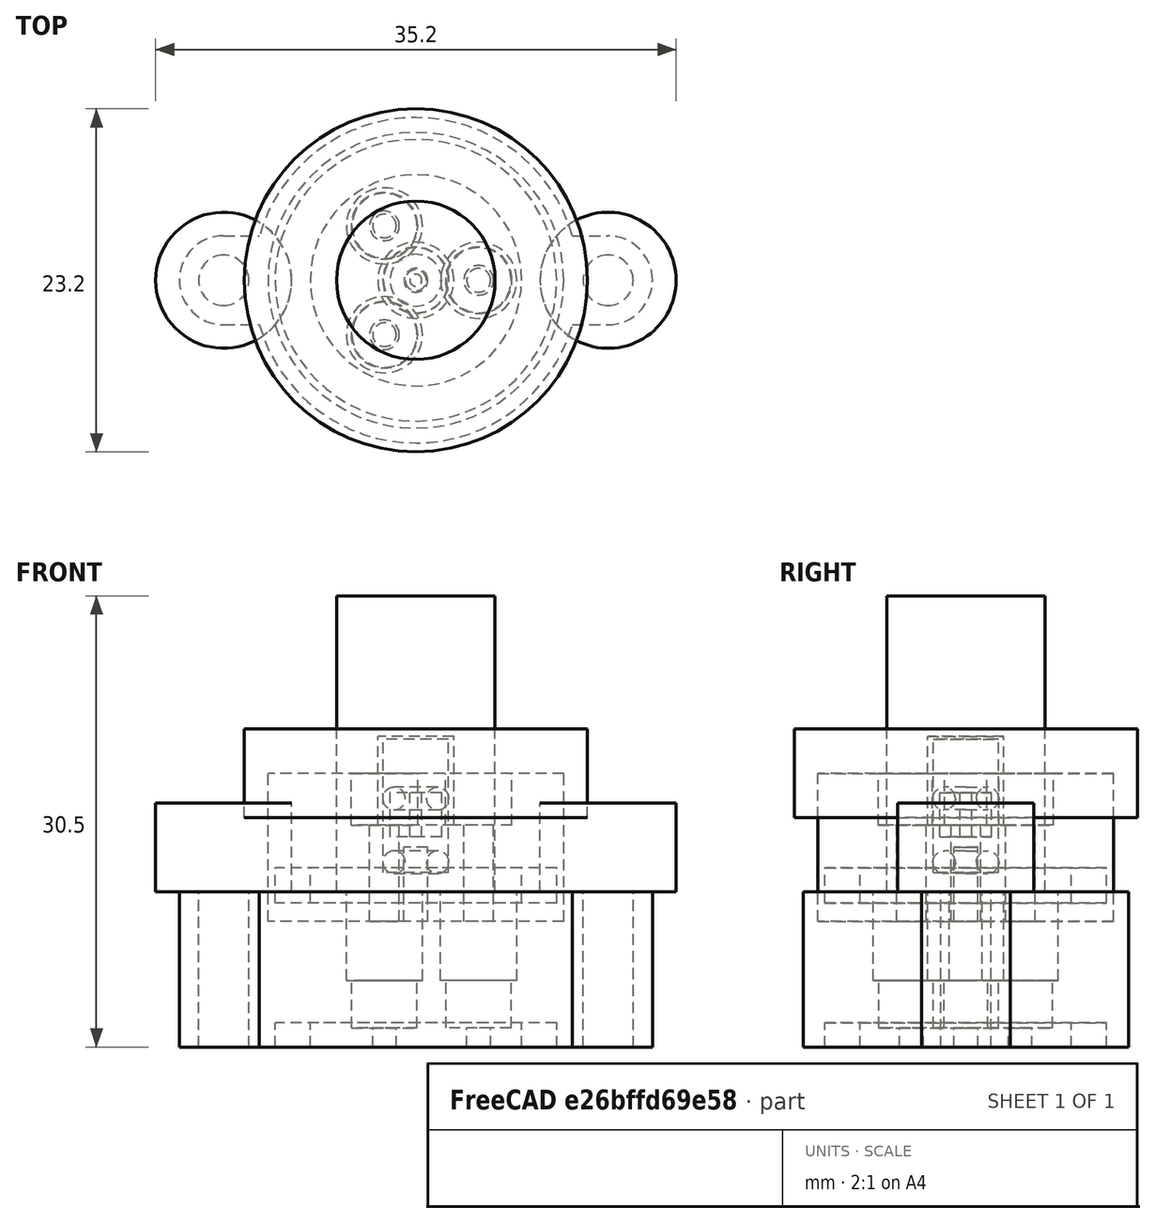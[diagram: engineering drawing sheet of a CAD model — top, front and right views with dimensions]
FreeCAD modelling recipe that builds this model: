
FCSTD DOCUMENT  (FreeCAD 0.17R13509 (Git))
Label: ceramic_wire_feedthroughs_insert_tall
License: All rights reserved
LicenseURL: http://en.wikipedia.org/wiki/All_rights_reserved
objects: Part::Cylinder×45, Part::MultiFuse×10, Part::Cut×9, Part::Box×6, Part::FeaturePython×4, Part::Feature×2, App::FeaturePython×1
note: 76 computed .brp shape members not serialized (recipe doc carries the construction recipe); baked Part::Feature solids carry a one-line shape summary decoded from their .brp

FEATURE [Part::Cylinder] Cylinder155  label="Cylinder009"
  Angle = 360
  AttacherType = Attacher::AttachEngine3D
  Height = 2.38125
  Radius = 9.525
  expr: Radius = 3 / 4 * 25.399999999999999 / 2
  expr: Height = 3 / 32 * 25.399999999999999
FEATURE [Part::Cylinder] Cylinder154  label="Cylinder008"
  Angle = 360
  AttacherType = Attacher::AttachEngine3D
  Height = 2.38125
  Radius = 7.14375
  expr: Radius = 9 / 16 * 25.399999999999999 / 2
  expr: Height = 3 / 32 * 25.399999999999999
FEATURE [Part::Feature] Part__Feature001  label="TopOring"
  Placement = pos=(0,0,6.3) rot=(0,0,1;0rad)
  shape: bbox 4.839 x 4.839 x 1.524 mm, 4 faces (baked)
FEATURE [Part::Feature] Part__Feature002  label="BottomOring"
  Placement = pos=(0,0,2) rot=(0,0,1;0rad)
  shape: bbox 4.839 x 4.839 x 1.524 mm, 4 faces (baked)
FEATURE [Part::Cylinder] Cylinder153  label="Body"
  Angle = 360
  AttacherType = Attacher::AttachEngine3D
  Height = 10
  Placement = pos=(0,0,-2) rot=(0,0,1;0rad)
  Radius = 10
FEATURE [Part::Cut] Cut019  label="Oring"
  Base = -> Cylinder155
  Placement = pos=(0,0,-0.75) rot=(0,0,1;0rad)
  Tool = -> Cylinder154
FEATURE [Part::Cylinder] Cylinder147  label="ThreadedSection"
  Angle = 360
  AttacherType = Attacher::AttachEngine3D
  Height = 1
  Placement = pos=(0,0,4.5) rot=(0,0,1;0rad)
  Radius = 1
FEATURE [Part::Cylinder] Cylinder149  label="FTBead"
  Angle = 360
  AttacherType = Attacher::AttachEngine3D
  Height = 3
  Placement = pos=(0,0,2.7) rot=(0,0,1;0rad)
  Radius = 1.75
  expr: Radius = 3.5 / 2
FEATURE [Part::Cylinder] Cylinder152  label="RFFeeds005"
  Angle = 360
  AttacherType = Attacher::AttachEngine3D
  Height = 20
  Radius = 5.35813
  expr: Placement.Base.x = 0
FEATURE [Part::Cylinder] Cylinder156  label="BottomWireOutlet"
  Angle = 360
  AttacherType = Attacher::AttachEngine3D
  Height = 14
  Placement = pos=(0,0,-7) rot=(0,0,1;0rad)
  Radius = 1
FEATURE [Part::Cylinder] Cylinder157  label="SealSubtraction"
  Angle = 360
  AttacherType = Attacher::AttachEngine3D
  Height = 7
  Placement = pos=(0,0,4.5) rot=(0,0,1;0rad)
  Radius = 2.25
FEATURE [Part::MultiFuse] Fusion
  Placement = pos=(4.25,0,0) rot=(0,0,1;0rad)
  Shapes = -> [Cylinder147,Cylinder157,Cylinder156]
FEATURE [Part::FeaturePython] Array  label="SealArray"  # Draft array (typed FeaturePython)
  Angle = 360
  ArrayType = 1
  Axis = (0,0,1)
  Base = -> Fusion
  Center = (0,0,0)
  Fuse = false
  IntervalAxis = (0,0,0)
  IntervalX = (1,0,0)
  IntervalY = (0,1,0)
  IntervalZ = (0,0,0)
  NumberPolar = 3
  NumberX = 2
  NumberY = 2
  NumberZ = 1
FEATURE [Part::Cylinder] Cylinder159  label="FTBeadHole"
  Angle = 360
  AttacherType = Attacher::AttachEngine3D
  Height = 17
  Radius = 0.405
  expr: Radius = 0.81000000000000005 / 2
FEATURE [Part::Cut] Cut020
  Base = -> Cylinder149
  Placement = pos=(0,0,1) rot=(0,0,1;0rad)
  Tool = -> Cylinder159
FEATURE [Part::Cylinder] Cylinder160  label="Cylinder010"
  Angle = 360
  AttacherType = Attacher::AttachEngine3D
  Height = 2.38125
  Radius = 9.525
  expr: Radius = 3 / 4 * 25.399999999999999 / 2
  expr: Height = 3 / 32 * 25.399999999999999
FEATURE [Part::Cylinder] Cylinder161  label="WireFeedsMount003"
  Angle = 360
  AttacherType = Attacher::AttachEngine3D
  Height = 11
  Placement = pos=(-13,0,0) rot=(0,0,1;0rad)
  Radius = 1.7
FEATURE [Part::Cylinder] Cylinder162  label="ThreadedSection001"
  Angle = 360
  AttacherType = Attacher::AttachEngine3D
  Height = 6
  Placement = pos=(0,0,4.5) rot=(0,0,1;0rad)
  Radius = 2.575
  expr: Radius = 5.1500000000000004 / 2
FEATURE [Part::Cylinder] Cylinder163  label="Cylinder011"
  Angle = 360
  AttacherType = Attacher::AttachEngine3D
  Height = 2.38125
  Radius = 7.14375
  expr: Radius = 9 / 16 * 25.399999999999999 / 2
  expr: Height = 3 / 32 * 25.399999999999999
FEATURE [Part::Cut] Cut022  label="Oring001"
  Base = -> Cylinder160
  Placement = pos=(0,0,-0.75) rot=(0,0,1;0rad)
  Tool = -> Cylinder163
FEATURE [Part::Cylinder] Cylinder164  label="Body001"
  Angle = 360
  AttacherType = Attacher::AttachEngine3D
  Height = 10.5
  Radius = 11
FEATURE [Part::Cylinder] Cylinder165  label="WireFeedsMount004"
  Angle = 360
  AttacherType = Attacher::AttachEngine3D
  Height = 11
  Placement = pos=(13,0,0) rot=(0,0,1;0rad)
  Radius = 1.7
FEATURE [Part::Cylinder] Cylinder166  label="BottomWireOutlet001"
  Angle = 360
  AttacherType = Attacher::AttachEngine3D
  Height = 5
  Placement = pos=(0,0,-2) rot=(0,0,1;0rad)
  Radius = 0.8
FEATURE [Part::Cylinder] Cylinder167  label="SealSubtraction001"
  Angle = 360
  AttacherType = Attacher::AttachEngine3D
  Height = 9
  Placement = pos=(0,0,1.3) rot=(0,0,1;0rad)
  Radius = 2.2
FEATURE [Part::Box] Box002  label="MountCube003"
  AttacherType = Attacher::AttachEngine3D
  Height = 10.5
  Length = 3
  Placement = pos=(10,-3,0) rot=(0,0,1;0rad)
  Width = 6
FEATURE [Part::Box] Box003  label="MountCube004"
  AttacherType = Attacher::AttachEngine3D
  Height = 10.5
  Length = 3
  Placement = pos=(-13,-3,0) rot=(0,0,1;0rad)
  Width = 6
FEATURE [Part::MultiFuse] Fusion004
  Placement = pos=(4.25,0,0) rot=(0,0,1;0rad)
  Shapes = -> [Cylinder162,Cylinder167,Cylinder166]
FEATURE [Part::Cylinder] Cylinder168  label="MountFlange003"
  Angle = 360
  AttacherType = Attacher::AttachEngine3D
  Height = 10.5
  Placement = pos=(-13,0,0) rot=(0,0,1;0rad)
  Radius = 3
FEATURE [Part::Cylinder] Cylinder169  label="MountFlange004"
  Angle = 360
  AttacherType = Attacher::AttachEngine3D
  Height = 10.5
  Placement = pos=(13,0,0) rot=(0,0,1;0rad)
  Radius = 3
FEATURE [Part::MultiFuse] Fusion003
  Shapes = -> [Cylinder169,Box002,Box003,Cylinder168,Cylinder164]
FEATURE [Part::FeaturePython] Array001  label="SealArray001"  # Draft array (typed FeaturePython)
  Angle = 360
  ArrayType = 1
  Axis = (0,0,1)
  Base = -> Fusion004
  Center = (0,0,0)
  Fuse = false
  IntervalAxis = (0,0,0)
  IntervalX = (1,0,0)
  IntervalY = (0,1,0)
  IntervalZ = (0,0,0)
  NumberPolar = 3
  NumberX = 2
  NumberY = 2
  NumberZ = 1
FEATURE [Part::MultiFuse] Fusion005
  Shapes = -> [Cylinder165,Cylinder161,Cut022,Array001]
FEATURE [Part::Cut] Cut021
  Base = -> Fusion003
  Placement = pos=(0,0,-10.5) rot=(0,0,1;0rad)
  Tool = -> Fusion005
FEATURE [Part::Cylinder] Cylinder170  label="Cylinder012"
  Angle = 360
  AttacherType = Attacher::AttachEngine3D
  Height = 2.38125
  Radius = 9.525
  expr: Radius = 3 / 4 * 25.399999999999999 / 2
  expr: Height = 3 / 32 * 25.399999999999999
FEATURE [Part::Cylinder] Cylinder171  label="WireFeedsMount005"
  Angle = 360
  AttacherType = Attacher::AttachEngine3D
  Height = 11
  Placement = pos=(-13,0,0) rot=(0,0,1;0rad)
  Radius = 1.7
FEATURE [Part::Cylinder] Cylinder172  label="ThreadedSection002"
  Angle = 360
  AttacherType = Attacher::AttachEngine3D
  Height = 6
  Placement = pos=(0,0,4.5) rot=(0,0,1;0rad)
  Radius = 2.575
  expr: Radius = 5.1500000000000004 / 2
FEATURE [Part::Cylinder] Cylinder173  label="Cylinder013"
  Angle = 360
  AttacherType = Attacher::AttachEngine3D
  Height = 2.38125
  Radius = 7.14375
  expr: Radius = 9 / 16 * 25.399999999999999 / 2
  expr: Height = 3 / 32 * 25.399999999999999
FEATURE [Part::Cut] Cut024  label="Oring002"
  Base = -> Cylinder170
  Placement = pos=(0,0,-0.75) rot=(0,0,1;0rad)
  Tool = -> Cylinder173
FEATURE [Part::Cylinder] Cylinder174  label="Body002"
  Angle = 360
  AttacherType = Attacher::AttachEngine3D
  Height = 10.5
  Radius = 11
FEATURE [Part::Cylinder] Cylinder175  label="WireFeedsMount006"
  Angle = 360
  AttacherType = Attacher::AttachEngine3D
  Height = 11
  Placement = pos=(13,0,0) rot=(0,0,1;0rad)
  Radius = 1.7
FEATURE [Part::Cylinder] Cylinder176  label="BottomWireOutlet002"
  Angle = 360
  AttacherType = Attacher::AttachEngine3D
  Height = 5
  Placement = pos=(0,0,-2) rot=(0,0,1;0rad)
  Radius = 0.8
FEATURE [Part::Cylinder] Cylinder177  label="SealSubtraction002"
  Angle = 360
  AttacherType = Attacher::AttachEngine3D
  Height = 9
  Placement = pos=(0,0,1.3) rot=(0,0,1;0rad)
  Radius = 2.2
FEATURE [Part::Box] Box004  label="MountCube005"
  AttacherType = Attacher::AttachEngine3D
  Height = 10.5
  Length = 3
  Placement = pos=(10,-3,0) rot=(0,0,1;0rad)
  Width = 6
FEATURE [App::FeaturePython] SetupSheet002  # Path/CAM operation (typed FeaturePython)
  ClearanceHeightExpression = StartDepth+SetupSheet.ClearanceHeightOffset
  ClearanceHeightOffset = 5
  FinalDepthExpression = OpFinalDepth
  HorizRapid = 0
  SafeHeightExpression = StartDepth+SetupSheet.SafeHeightOffset
  SafeHeightOffset = 3
  StartDepthExpression = OpStartDepth
  StepDownExpression = OpToolDiameter
  VertRapid = 0
FEATURE [Part::Box] Box005  label="MountCube006"
  AttacherType = Attacher::AttachEngine3D
  Height = 10.5
  Length = 3
  Placement = pos=(-13,-3,0) rot=(0,0,1;0rad)
  Width = 6
FEATURE [Part::MultiFuse] Fusion007
  Placement = pos=(4.25,0,0) rot=(0,0,1;0rad)
  Shapes = -> [Cylinder172,Cylinder177,Cylinder176]
FEATURE [Part::Cylinder] Cylinder178  label="MountFlange005"
  Angle = 360
  AttacherType = Attacher::AttachEngine3D
  Height = 10.5
  Placement = pos=(-13,0,0) rot=(0,0,1;0rad)
  Radius = 3
FEATURE [Part::Cylinder] Cylinder179  label="MountFlange006"
  Angle = 360
  AttacherType = Attacher::AttachEngine3D
  Height = 10.5
  Placement = pos=(13,0,0) rot=(0,0,1;0rad)
  Radius = 3
FEATURE [Part::MultiFuse] Fusion006
  Shapes = -> [Cylinder179,Box004,Box005,Cylinder178,Cylinder174]
FEATURE [Part::FeaturePython] Array002  label="SealArray002"  # Draft array (typed FeaturePython)
  Angle = 360
  ArrayType = 1
  Axis = (0,0,1)
  Base = -> Fusion007
  Center = (0,0,0)
  Fuse = false
  IntervalAxis = (0,0,0)
  IntervalX = (1,0,0)
  IntervalY = (0,1,0)
  IntervalZ = (0,0,0)
  NumberPolar = 3
  NumberX = 2
  NumberY = 2
  NumberZ = 1
FEATURE [Part::MultiFuse] Fusion008
  Shapes = -> [Cylinder175,Cylinder171,Cut024,Array002]
FEATURE [Part::Cut] Cut023
  Base = -> Fusion006
  Placement = pos=(0,0,-10.5) rot=(0,0,1;0rad)
  Tool = -> Fusion008
FEATURE [Part::Cylinder] Cylinder180  label="Cylinder014"
  Angle = 360
  AttacherType = Attacher::AttachEngine3D
  Height = 2.38125
  Radius = 7.14375
  expr: Radius = 9 / 16 * 25.399999999999999 / 2
  expr: Height = 3 / 32 * 25.399999999999999
FEATURE [Part::Cylinder] Cylinder181  label="MountFlange007"
  Angle = 360
  AttacherType = Attacher::AttachEngine3D
  Height = 10.5
  Placement = pos=(-13,0,0) rot=(0,0,1;0rad)
  Radius = 3
FEATURE [Part::Box] Box006  label="MountCube007"
  AttacherType = Attacher::AttachEngine3D
  Height = 10.5
  Length = 3
  Placement = pos=(-13,-3,0) rot=(0,0,1;0rad)
  Width = 6
FEATURE [Part::Cylinder] Cylinder182  label="WireFeedsMount007"
  Angle = 360
  AttacherType = Attacher::AttachEngine3D
  Height = 11
  Placement = pos=(13,0,0) rot=(0,0,1;0rad)
  Radius = 1.7
FEATURE [Part::Box] Box007  label="MountCube008"
  AttacherType = Attacher::AttachEngine3D
  Height = 10.5
  Length = 3
  Placement = pos=(10,-3,0) rot=(0,0,1;0rad)
  Width = 6
FEATURE [Part::Cylinder] Cylinder183  label="WireFeedsMount008"
  Angle = 360
  AttacherType = Attacher::AttachEngine3D
  Height = 11
  Placement = pos=(-13,0,0) rot=(0,0,1;0rad)
  Radius = 1.7
FEATURE [Part::Cylinder] Cylinder184  label="Body003"
  Angle = 360
  AttacherType = Attacher::AttachEngine3D
  Height = 10.5
  Radius = 11
FEATURE [Part::Cylinder] Cylinder185  label="MountFlange008"
  Angle = 360
  AttacherType = Attacher::AttachEngine3D
  Height = 10.5
  Placement = pos=(13,0,0) rot=(0,0,1;0rad)
  Radius = 3
FEATURE [Part::Cylinder] Cylinder186  label="BottomWireOutlet003"
  Angle = 360
  AttacherType = Attacher::AttachEngine3D
  Height = 5
  Placement = pos=(0,0,-2) rot=(0,0,1;0rad)
  Radius = 0.8
FEATURE [Part::MultiFuse] Fusion011
  Shapes = -> [Cylinder185,Box007,Box006,Cylinder181,Cylinder184]
FEATURE [Part::Cylinder] Cylinder187  label="ThreadedSection003"
  Angle = 360
  AttacherType = Attacher::AttachEngine3D
  Height = 6
  Placement = pos=(0,0,4.5) rot=(0,0,1;0rad)
  Radius = 2.575
  expr: Radius = 5.1500000000000004 / 2
FEATURE [Part::Cylinder] Cylinder188  label="Cylinder015"
  Angle = 360
  AttacherType = Attacher::AttachEngine3D
  Height = 2.38125
  Radius = 9.525
  expr: Radius = 3 / 4 * 25.399999999999999 / 2
  expr: Height = 3 / 32 * 25.399999999999999
FEATURE [Part::Cut] Cut025  label="Oring003"
  Base = -> Cylinder188
  Placement = pos=(0,0,-0.75) rot=(0,0,1;0rad)
  Tool = -> Cylinder180
FEATURE [Part::Cylinder] Cylinder189  label="SealSubtraction003"
  Angle = 360
  AttacherType = Attacher::AttachEngine3D
  Height = 9
  Placement = pos=(0,0,1.3) rot=(0,0,1;0rad)
  Radius = 2.2
FEATURE [Part::MultiFuse] Fusion009
  Placement = pos=(4.25,0,0) rot=(0,0,1;0rad)
  Shapes = -> [Cylinder187,Cylinder189,Cylinder186]
FEATURE [Part::FeaturePython] Array003  label="SealArray003"  # Draft array (typed FeaturePython)
  Angle = 360
  ArrayType = 1
  Axis = (0,0,1)
  Base = -> Fusion009
  Center = (0,0,0)
  Fuse = false
  IntervalAxis = (0,0,0)
  IntervalX = (1,0,0)
  IntervalY = (0,1,0)
  IntervalZ = (0,0,0)
  NumberPolar = 3
  NumberX = 2
  NumberY = 2
  NumberZ = 1
FEATURE [Part::MultiFuse] Fusion010
  Shapes = -> [Cylinder182,Cylinder183,Cut025,Array003]
FEATURE [Part::Cut] Cut026
  Base = -> Fusion011
  Placement = pos=(0,0,-10.5) rot=(0,0,1;0rad)
  Tool = -> Fusion010
FEATURE [Part::Cylinder] Cylinder192  label="ThreadedSection004"
  Angle = 360
  AttacherType = Attacher::AttachEngine3D
  Height = 6
  Placement = pos=(0,0,4.5) rot=(0,0,1;0rad)
  Radius = 2.575
  expr: Radius = 5.1500000000000004 / 2
FEATURE [Part::Cylinder] Cylinder196  label="BottomWireOutlet004"
  Angle = 360
  AttacherType = Attacher::AttachEngine3D
  Height = 5
  Placement = pos=(0,0,-2) rot=(0,0,1;0rad)
  Radius = 0.8
FEATURE [Part::Cylinder] Cylinder197  label="SealSubtraction004"
  Angle = 360
  AttacherType = Attacher::AttachEngine3D
  Height = 9
  Placement = pos=(0,0,1.3) rot=(0,0,1;0rad)
  Radius = 2.2
FEATURE [Part::Cylinder] Cylinder198  label="Cylinder"
  Angle = 360
  AttacherType = Attacher::AttachEngine3D
  Height = 6
  Placement = pos=(0,0,5) rot=(0,0,1;0rad)
  Radius = 11.6
FEATURE [Part::Cylinder] Cylinder199  label="Cylinder016"
  Angle = 360
  AttacherType = Attacher::AttachEngine3D
  Height = 6
  Placement = pos=(-13,0,0) rot=(0,0,1;0rad)
  Radius = 4.6
FEATURE [Part::Cylinder] Cylinder200  label="Cylinder017"
  Angle = 360
  AttacherType = Attacher::AttachEngine3D
  Height = 6
  Placement = pos=(13,0,0) rot=(0,0,1;0rad)
  Radius = 4.6
FEATURE [Part::Cut] Cut
  Base = -> Cylinder153
  Tool = -> Array
